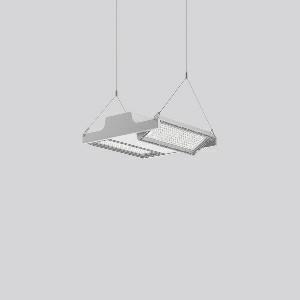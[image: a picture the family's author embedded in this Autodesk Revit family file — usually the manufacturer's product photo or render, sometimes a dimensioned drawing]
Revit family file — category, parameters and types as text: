
# Revit family: light_case_921681_004_1_76_0436
name_source: partatom
category: Lighting Fixtures
units: mm (PartAtom-declared; Revit-internal decimal feet)

## family parameters
Cut with Voids When Loaded = No
Host = Face
Light Source = No
Part Type = Normal
Room Calculation Point = No
Round Connector Dimension = Use Diameter
Shared = No

## types (1)
- LIGHT CASE (1 x LED Modul 865, 8700 lm, 6500)
    Apparent Load = 117 VA
    CIE Flux Codes = 85 97 100 100 100
    Color Rendering = 80
    Color Temperature = 6500
    Default Elevation = 1800 mm
    Description = Series: LIGHT CASE
Flat highbay luminaire for chain or cable suspension with 2 LED modules that can be swivelled. Housing: die cast aluminium and sheet steel, powder-coated. Optimised thermal management thanks to special luminaire design. Self-cleaning heat sink for constant heat dissipation. Cover: plastic (polycarbonate, shockproof), with integrated four-row lens system. LED modules can be swivelled ± 30° for optimum illumination. Suitable for chain or steel cable suspension (to be provided on site). With 5-pin connection terminal (1.5 m). With integrated movement sensor and light sensor for daylight detection on request. Ball impact proof in accordance with DIN 18032-03 (except steel cable suspension). Luminaire with limited surface temperature in accordance with EN 60598-2-24 for use in environments in which a deposit of conductive dust on the luminaire can be expected. 
Colour: silver, matt (approx. RAL 9006)
Length: 406 mm
Width: 397 mm
Height: 110 mm
Lamp: LED
Socket: without socket
Colour temperature: 6500K
Colour rendering index (CRI): 80
System power: 117 W
Rated luminous flux: 17400 lm
Luminous efficiency: 149 lm/W
Control gear: Converter, dimmable, DALI
Protection class: I
Type of protection: IP 65
    Height = 110 mm
    Lamp = 1 x LED Modul 865
    Lamp Light Flux = 8700 lm
    Lamp count = 1
    Length = 406 mm
    Lifetime = 50000 h
    Luminous efficacy = 149 lm/W
    Manufacturer = RZB
    ModVariant = No
    Model = 921681.004.1.76
    Mounting Place = Ceiling
    Mounting Type = Pendant
    Number of Poles = 1
    OnlyDefault = Yes
    Power Factor = 1
    Product Name = LIGHT CASE
    Product group = Pendant commercial luminaires
    ProductGroupID = 903
    Protection Class = Protection class I
    Protection Degree = IP 65
    RLX_Detail_Level = 1
    RLX_Emergency_Light_Flux = 0 lm
    RLX_Emergency_Type = 0
    RLX_Emergency_Type_DB = No
    RlxData = <blob elided: 26121 chars, md5=e5eb4703>
    Socket = socket
    Standby Power = 0 W
    System Light Flux = 17400 lm
    System Power = 117 W
    Type Comments = Product without accessories
    Type Image = 921517.004.76.jpg
    URL = http://relux.com
    VarID = ---
    Voltage = 230 V
    Voltage Range = 220-240 V
    Weight = 0.00 kg
    Width = 397 mm

## geometry (parser evidence)
native form markers: Blend x4, Sweep x18
no freeform markers — native parametric forms only
